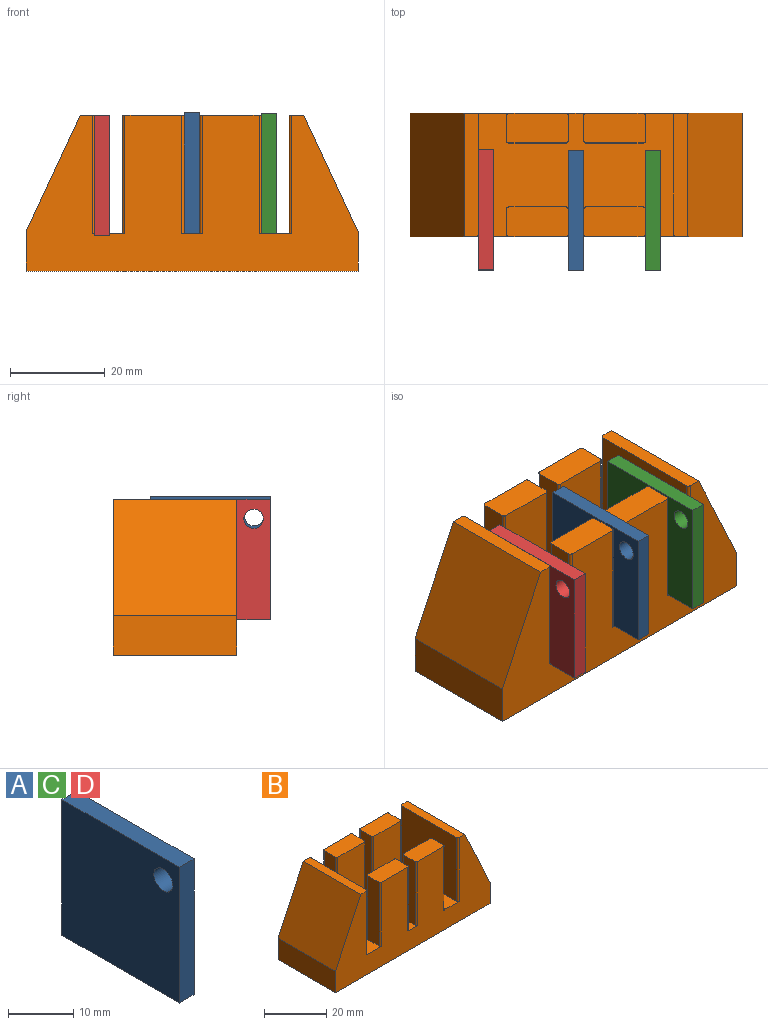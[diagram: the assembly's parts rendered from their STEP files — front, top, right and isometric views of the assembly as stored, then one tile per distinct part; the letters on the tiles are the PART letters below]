
ASSEMBLY  parts=4 mates=3
PART A: 7 faces, bbox 3.2x25.4x25.4 mm
  f0: plane 25.4x3.18mm, normal (0,0,1), area 80.6mm2, adj f1,f4,f5,f6
  f1: plane 25.4x3.18mm, normal (0,-1,0), area 80.6mm2, adj f0,f2,f5,f6
  f2: plane 25.4x3.18mm, normal (0,0,-1), area 80.6mm2, adj f1,f4,f5,f6
  f3: cylinder r=2.04mm len=4.08mm, axis (-1,0,0), area 40.7mm2, adj f5,f6
  f4: plane 25.4x3.18mm, normal (0,1,0), area 80.6mm2, adj f0,f2,f5,f6
  f5: plane 25.4x25.4mm, normal (1,0,0), area 632.1mm2, adj f0,f1,f2,f3,f4
  f6: plane 25.4x25.4mm, normal (-1,0,0), area 632.1mm2, adj f0,f1,f2,f3,f4
PART B: 48 faces, bbox 70x26x32.9 mm
  f0: plane 13x6.25mm, normal (0,0,1), area 81mm2, adj f5,f13,f17,f23,f30,f36,f46,f47
  f1: plane 13x6.25mm, normal (0,0,1), area 81mm2, adj f8,f14,f19,f25,f29,f37,f44,f45
  f2: plane 26x3.08mm, normal (0,0,1), area 79.9mm2, adj f5,f8,f21,f26,f32,f35
  f3: plane 13x6.25mm, normal (0,0,1), area 81mm2, adj f5,f12,f16,f20,f31,f33,f42,f43
  f4: plane 13x6.25mm, normal (0,0,1), area 81mm2, adj f8,f11,f18,f22,f28,f34,f40,f41
  f5: plane 70x32.86mm, normal (0,1,0), area 1569mm2, adj f0,f2,f3,f6,f7,f9,f10,f15
  f6: plane 26x3.08mm, normal (0,0,1), area 79.9mm2, adj f5,f8,f24,f27,f38,f39
  f7: plane 26x8.35mm, normal (-1,0,0), area 217mm2, adj f5,f8,f10,f27
  f8: plane 70x32.86mm, normal (0,-1,0), area 1569mm2, adj f1,f2,f4,f6,f7,f9,f10,f15
  f9: plane 26x8.35mm, normal (1,0,0), area 217mm2, adj f5,f8,f10,f26
  f10: plane 70x26mm, normal (0,0,-1), area 1820mm2, adj f5,f7,f8,f9
  f11: plane 25x11.98mm, normal (0,1,0), area 299.6mm2, adj f4,f15,f40,f41
  f12: plane 25x11.98mm, normal (0,-1,0), area 299.6mm2, adj f3,f15,f42,f43
  f13: plane 25x11.98mm, normal (0,-1,0), area 299.6mm2, adj f0,f15,f46,f47
  f14: plane 25x11.98mm, normal (0,1,0), area 299.6mm2, adj f1,f15,f44,f45
  f15: plane 42x26mm, normal (0,0,1), area 741.7mm2, adj f5,f8,f11,f12,f13,f14,f16,f17
  f16: plane 25x5.23mm, normal (-1,0,0), area 130.8mm2, adj f3,f15,f31,f43
  f17: plane 25x5.23mm, normal (1,0,0), area 130.8mm2, adj f0,f15,f30,f47
  f18: plane 25x5.23mm, normal (-1,0,0), area 130.8mm2, adj f4,f15,f28,f40
  f19: plane 25x5.23mm, normal (1,0,0), area 130.8mm2, adj f1,f15,f29,f44
  f20: plane 25x5.23mm, normal (1,0,0), area 130.8mm2, adj f3,f15,f33,f42
  f21: plane 25x24.98mm, normal (-1,0,0), area 624.6mm2, adj f2,f15,f32,f35
  f22: plane 25x5.23mm, normal (1,0,0), area 130.8mm2, adj f4,f15,f34,f41
  f23: plane 25x5.23mm, normal (-1,0,0), area 130.8mm2, adj f0,f15,f36,f46
  f24: plane 25x24.98mm, normal (1,0,0), area 624.6mm2, adj f6,f15,f38,f39
  f25: plane 25x5.23mm, normal (-1,0,0), area 130.8mm2, adj f1,f15,f37,f45
  f26: plane 26x24.51mm, normal (0.91,0,0.42), area 703.2mm2, adj f2,f5,f8,f9
  f27: plane 26x24.51mm, normal (-0.91,0,0.42), area 703.2mm2, adj f5,f6,f7,f8
  f28: cylinder r=0.51mm len=25mm, axis (0,0,-1), area 19.9mm2, adj f4,f8,f15,f18
  f29: cylinder r=0.51mm len=25mm, axis (0,0,1), area 19.9mm2, adj f1,f8,f15,f19
  f30: cylinder r=0.51mm len=25mm, axis (0,0,-1), area 19.9mm2, adj f0,f5,f15,f17
  f31: cylinder r=0.51mm len=25mm, axis (0,0,1), area 19.9mm2, adj f3,f5,f15,f16
  f32: cylinder r=0.51mm len=25mm, axis (0,0,1), area 19.9mm2, adj f2,f5,f15,f21
  f33: cylinder r=0.51mm len=25mm, axis (0,0,-1), area 19.9mm2, adj f3,f5,f15,f20
  f34: cylinder r=0.51mm len=25mm, axis (0,0,1), area 19.9mm2, adj f4,f8,f15,f22
  f35: cylinder r=0.51mm len=25mm, axis (0,0,-1), area 19.9mm2, adj f2,f8,f15,f21
  f36: cylinder r=0.51mm len=25mm, axis (0,0,1), area 19.9mm2, adj f0,f5,f15,f23
  f37: cylinder r=0.51mm len=25mm, axis (0,0,-1), area 19.9mm2, adj f1,f8,f15,f25
  f38: cylinder r=0.51mm len=25mm, axis (0,0,1), area 19.9mm2, adj f6,f8,f15,f24
  f39: cylinder r=0.51mm len=25mm, axis (0,0,-1), area 19.9mm2, adj f5,f6,f15,f24
  f40: cylinder r=0.51mm len=25mm, axis (0,0,1), area 19.9mm2, adj f4,f11,f15,f18
  f41: cylinder r=0.51mm len=25mm, axis (0,0,-1), area 19.9mm2, adj f4,f11,f15,f22
  f42: cylinder r=0.51mm len=25mm, axis (0,0,1), area 19.9mm2, adj f3,f12,f15,f20
  f43: cylinder r=0.51mm len=25mm, axis (0,0,-1), area 19.9mm2, adj f3,f12,f15,f16
  f44: cylinder r=0.51mm len=25mm, axis (0,0,-1), area 19.9mm2, adj f1,f14,f15,f19
  f45: cylinder r=0.51mm len=25mm, axis (0,0,1), area 19.9mm2, adj f1,f14,f15,f25
  f46: cylinder r=0.51mm len=25mm, axis (0,0,-1), area 19.9mm2, adj f0,f13,f15,f23
  f47: cylinder r=0.51mm len=25mm, axis (0,0,1), area 19.9mm2, adj f0,f13,f15,f17
PART C: same geometry as A
PART D: same geometry as A
PLACE A t=(27.08,16.43,-1.57)mm
PLACE B t=(-6.27,23.59,-6.67)mm
PLACE C t=(43.38,16.44,-1.69)mm
PLACE D t=(8.24,16.55,-2.09)mm
MATE planar B.f22 <-> C.f6  axis (1,0,0) through (43.38,29.33,10.83)mm
MATE planar D.f6 <-> B.f24  axis (-1,0,0) through (8.24,29.25,23.31)mm
MATE planar B.f19 <-> A.f3  axis (1,0,0) through (27.08,26.71,10.83)mm
